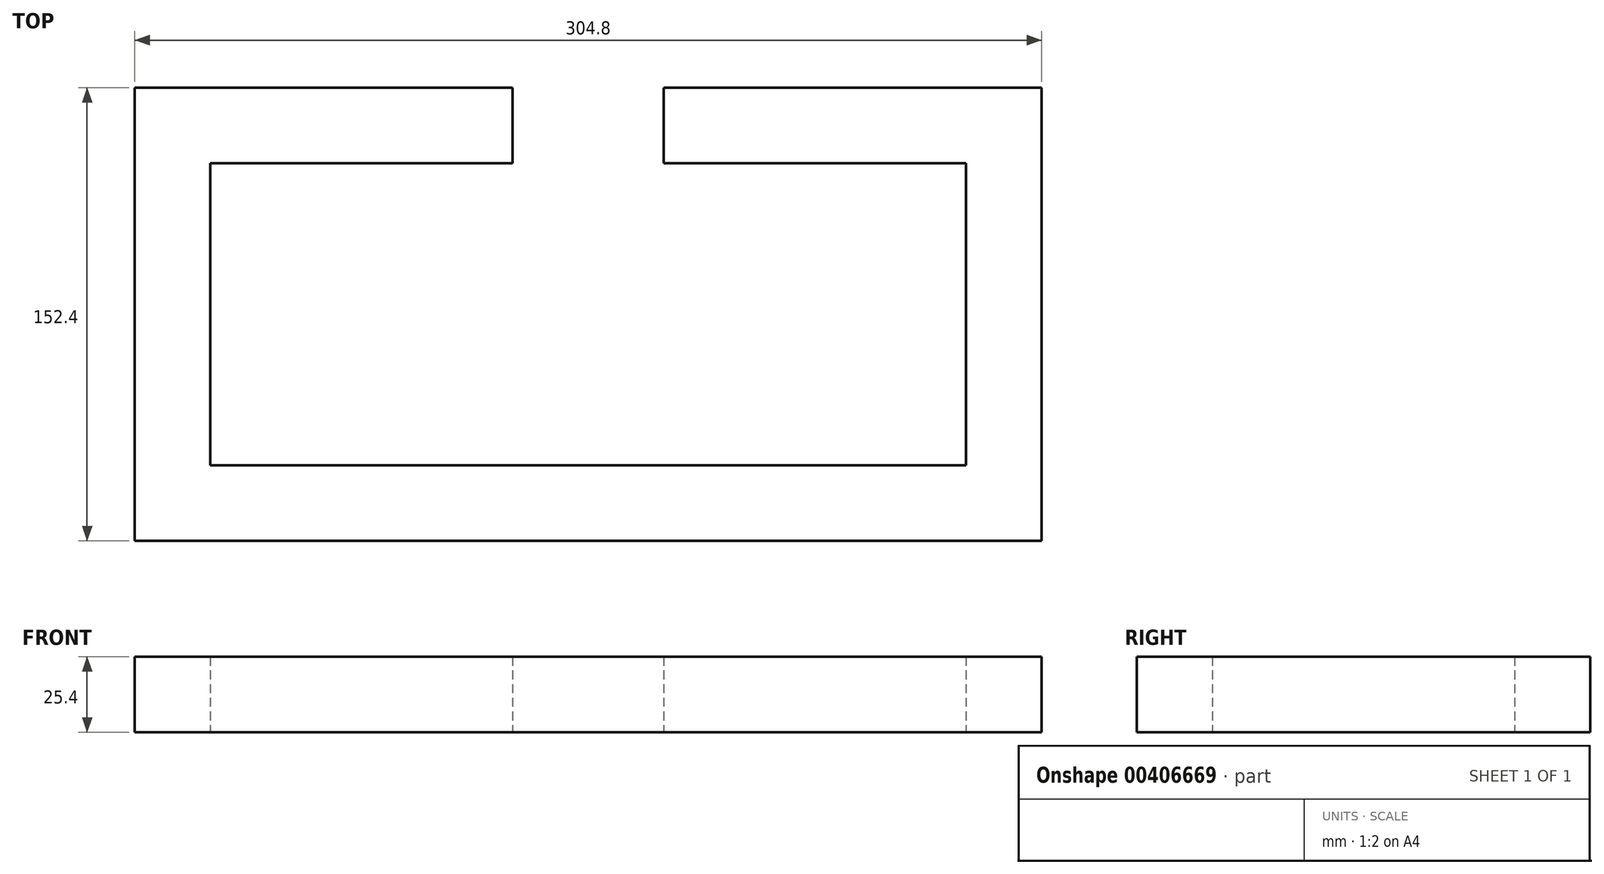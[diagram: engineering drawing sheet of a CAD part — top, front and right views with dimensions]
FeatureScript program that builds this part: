
annotation { "Feature Type Name" : "Feature", "Feature Type Description" : "" }
export const myFeature = defineFeature(function(context is Context, id is Id, definition is map)
    precondition{}
    {
        {
            var Q0;
            Q0=qCreatedBy(makeId("Top.planeOp"),FACE);
            var sketch = newSketch(context, id + "F0", { "sketchPlane" : qUnion([Q0])});
            skLineSegment(sketch, "E0.bottom", {"start": v(152.4, -76.2) * mm, "end": v(-152.4, -76.2) * mm});
            skLineSegment(sketch, "E0.top", {"start": v(152.4, 76.2) * mm, "end": v(25.4, 76.2) * mm});
            skLineSegment(sketch, "E0.left", {"start": v(152.4, -76.2) * mm, "end": v(152.4, 76.2) * mm});
            skLineSegment(sketch, "E0.right", {"start": v(-152.4, -76.2) * mm, "end": v(-152.4, 76.2) * mm});
            skPoint(sketch, "E0.middle", {"position": v(0, 0) * mm});
            skLineSegment(sketch, "E1.bottom", {"start": v(127, -50.8) * mm, "end": v(-127, -50.8) * mm});
            skLineSegment(sketch, "E1.top", {"start": v(127, 50.8) * mm, "end": v(25.4, 50.8) * mm});
            skLineSegment(sketch, "E1.left", {"start": v(127, -50.8) * mm, "end": v(127, 50.8) * mm});
            skLineSegment(sketch, "E1.right", {"start": v(-127, -50.8) * mm, "end": v(-127, 50.8) * mm});
            skPoint(sketch, "E2.start.orphan", {"position": v(0, 30.78) * mm});
            skLineSegment(sketch, "E3", {"start": v(-25.4, 50.8) * mm, "end": v(-25.4, 76.2) * mm});
            skLineSegment(sketch, "E4", {"start": v(25.4, 50.8) * mm, "end": v(25.4, 76.2) * mm});
            skLineSegment(sketch, "E5", {"start": v(-25.4, 76.2) * mm, "end": v(-25.4, 50.8) * mm});
            skPoint(sketch, "E5.endSnap0", {"position": v(-25.4, 53.49) * mm});
            skLineSegment(sketch, "E6", {"start": v(25.4, 76.2) * mm, "end": v(25.4, 50.8) * mm});
            skPoint(sketch, "E6.endSnap0", {"position": v(25.4, 53.49) * mm});
            skPoint(sketch, "E7.orphan", {"position": v(-25.4, 30.78) * mm});
            skPoint(sketch, "E8.orphan", {"position": v(25.4, 30.78) * mm});
            skLineSegment(sketch, "E9.trimOffspring", {"start": v(-25.4, 50.8) * mm, "end": v(-127, 50.8) * mm});
            skLineSegment(sketch, "E10.trimOffspring", {"start": v(-25.4, 76.2) * mm, "end": v(-152.4, 76.2) * mm});
            skLineSegment(sketch, "E11", {"start": v(0, 30.78) * mm, "end": v(-59.37, 30.78) * mm});
            skSolve(sketch);
        }
        {
            var Q0;
            Q0=makeQuery(id+"F0.imprint","IMPRINT",FACE,{"disambiguationData":[TD([[makeQuery(id+"F0.imprint","IMPRINT",EDGE,{"derivedFrom":sQuery(id+"F0.wireOp",EDGE,"E0.bottom")}),-1.0]])]});
            extrude(context, id + "F1", {"entities" : qUnion([Q0]), "depth" : 25.4 * mm, "offsetDistance" : 25.4 * mm});
        }
    });
